# Revit family: Alsanit - Kabiny sanitarne AQUARI - LPW
name_source: partatom
category: Doors
units: mm (PartAtom-declared; Revit-internal decimal feet)

## family parameters
Always vertical = Yes
Cut with Voids When Loaded = No
Room Calculation Point = No
Shared = No
Work Plane-Based = No

## types (1)
- 18mm
    Analytic Construction = <None>
    Autor = www.archispace.pl
    Construction Type = Kabiny sanitarne
    Default Elevation = 0 mm  [stored 0 ft]
    Define Thermal Properties by = Schematic Type
    Description = Kabiny sanitarne to idealna kombinacja trwałości i estetyki w najnowszej cenie. Ze względu na estetyczność zastosowań jest najchętniej kupowanym systemem kabin sanitarnych w Polsce.
    Film Instruktażowy = https://youtu.be
    Function = Interior
    Grubość ścianki = 18 mm  [stored 0.0590551 ft]
    Height = 0 mm  [stored 0 ft]
    Krótki opis = Kabiny sanitarne ALSANIT posiadające oznaczenie CE zgodnie z parametrami systemu
    Lewa strona połączona typ = Rodzaj połączenia : Połączona
    Lewa strona przy ścianie typ = Rodzaj połączenia : Przy ścianie
    Lewa strona zamknięta typ = Rodzaj połączenia : Zamknięta
    Manufacturer = Alsanit
    Materiał belek = Alsanit - Aluminium
    Materiał okuć = Alsanit - Aluminium
    Materiał płyt = Alsanit - LPW - Biały 9016
    Materiał wsporników = Alsanit - Aluminium
    Model = AQUARI
    Prawa strona połączona typ = Rodzaj połączenia : Połączona
    Prawa strona przy ścianie typ = Rodzaj połączenia : Przy ścianie
    Prawa strona zamknięta typ = Rodzaj połączenia : Zamknięta
    Rodzaj płyt = LPW - Laminowana płyta wiórowa
    Rough Height = 0 mm  [stored 0 ft]
    Rough Width = 0 mm  [stored 0 ft]
    Szczelina lewa 1 = 26 mm
    Szczelina lewa 2 = 23 mm  [stored 0.0754593 ft]
    Szczelina prawa 1 = 23 mm  [stored 0.0754593 ft]
    Szczelina prawa 2 = 26 mm
    Thickness = 18 mm  [stored 0.0590551 ft]
    Type Comments = Kabiny sanitarne (ścianki giszetowe do WC)
    URL = https://www.alsanit.pl
    Width = 0 mm  [stored 0 ft]

note: [stored X ft] marks values corroborated as IEEE doubles in the binary element streams (Revit-internal decimal feet)

## geometry (parser evidence)
native form markers: Sweep x8
no freeform markers — native parametric forms only
